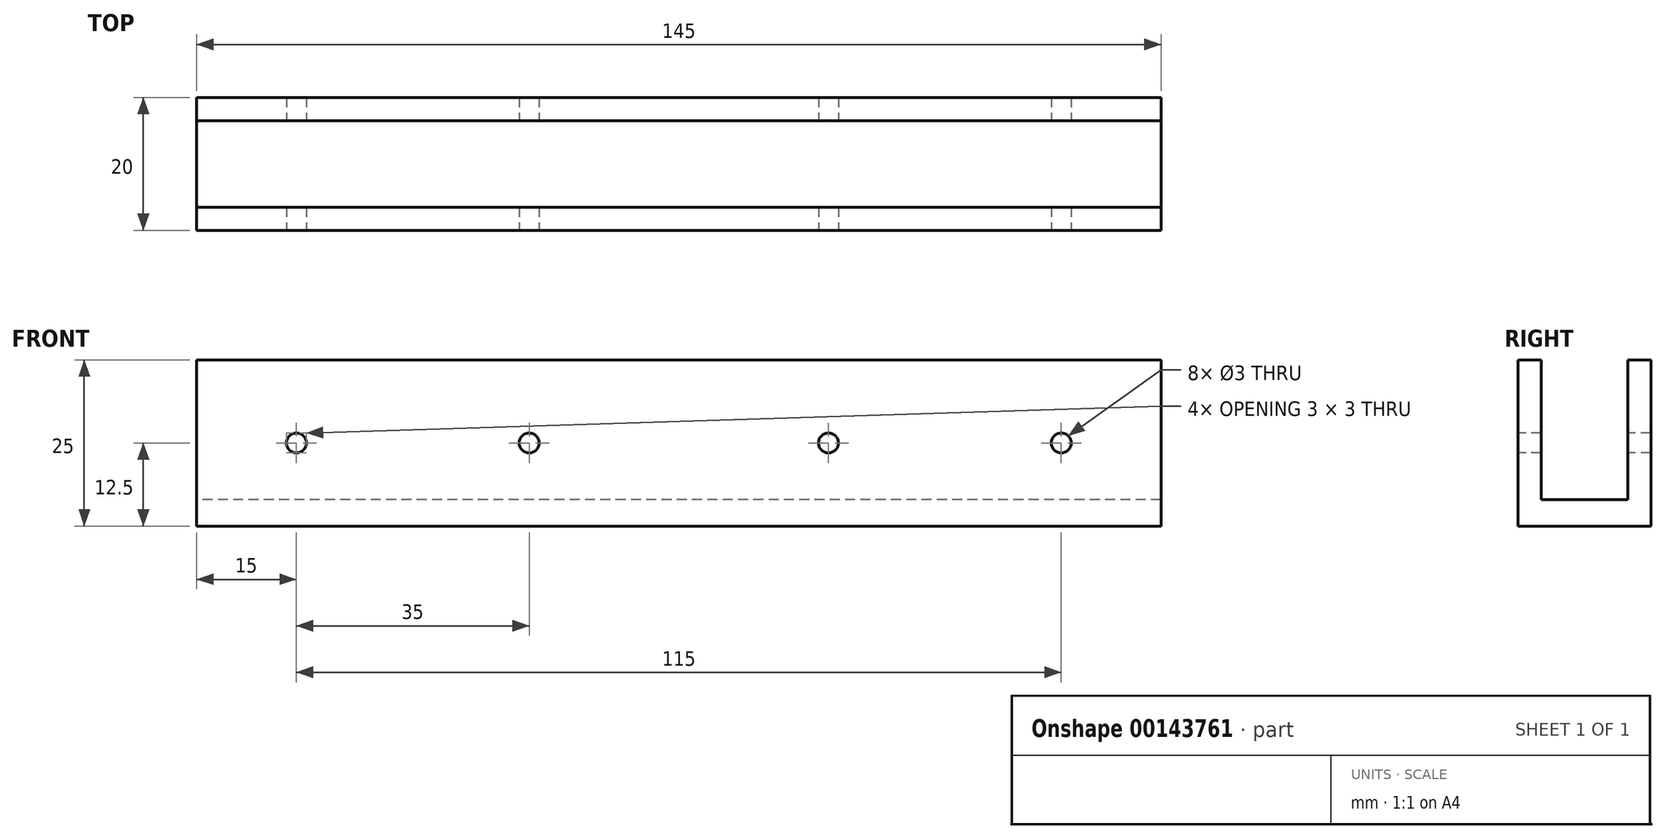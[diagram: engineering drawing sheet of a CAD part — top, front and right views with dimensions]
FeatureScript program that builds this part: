
annotation { "Feature Type Name" : "Feature", "Feature Type Description" : "" }
export const myFeature = defineFeature(function(context is Context, id is Id, definition is map)
    precondition{}
    {
        {
            var Q0;
            Q0=qCreatedBy(makeId("Right.planeOp"),FACE);
            var sketch = newSketch(context, id + "F0", { "sketchPlane" : qUnion([Q0])});
            skLineSegment(sketch, "E0", {"start": v(0, 0) * mm, "end": v(-10, 0) * mm});
            skLineSegment(sketch, "E1", {"start": v(-10, 0) * mm, "end": v(-10, 25) * mm});
            skLineSegment(sketch, "E2", {"start": v(-10, 25) * mm, "end": v(-6.5, 25) * mm});
            skLineSegment(sketch, "E3", {"start": v(-6.5, 25) * mm, "end": v(-6.5, 4) * mm});
            skLineSegment(sketch, "E4", {"start": v(-6.5, 4) * mm, "end": v(0, 4) * mm});
            skLineSegment(sketch, "E5.MirrorCS", {"start": v(6.5, 4) * mm, "end": v(0, 4) * mm});
            skLineSegment(sketch, "E6.MirrorCS", {"start": v(6.5, 25) * mm, "end": v(6.5, 4) * mm});
            skLineSegment(sketch, "E7.MirrorCS", {"start": v(10, 25) * mm, "end": v(6.5, 25) * mm});
            skLineSegment(sketch, "E8.MirrorCS", {"start": v(10, 0) * mm, "end": v(10, 25) * mm});
            skLineSegment(sketch, "E9.MirrorCS", {"start": v(0, 0) * mm, "end": v(10, 0) * mm});
            skSolve(sketch);
        }
        {
            var Q0;
            Q0 = qSketchRegion(id + "F0", true);
            extrude(context, id + "F1", {"entities" : qUnion([Q0]), "depth" : 145 * mm});
        }
        {
            var Q0;
            Q0=makeQuery(id+"F1.opExtrude","SWEPT_FACE",FACE,{"disambiguationData":[OSD([sQuery(id+"F0.wireOp",EDGE,"E1")])]});
            var sketch = newSketch(context, id + "F2", { "sketchPlane" : qUnion([Q0])});
            skCircle(sketch, "E10", {"center": v(15, 12.5) * mm, "radius": 1.8 * mm});
            skPoint(sketch, "E10.centerSnap0", {"position": v(0, 12.5) * mm});
            skCircle(sketch, "E11", {"center": v(50, 12.5) * mm, "radius": 2.4 * mm});
            skCircle(sketch, "E12", {"center": v(130, 12.5) * mm, "radius": 1.6 * mm});
            skCircle(sketch, "E13", {"center": v(95, 12.5) * mm, "radius": 1.81 * mm});
            skSolve(sketch);
        }
        {
            var Q0;
            Q0=sQuery(id+"F2.wireOp",VERTEX,"E10.center");
            var Q1;
            Q1=sQuery(id+"F2.wireOp",VERTEX,"E11.center");
            var Q2;
            Q2=sQuery(id+"F2.wireOp",VERTEX,"E13.center");
            var Q3;
            Q3=sQuery(id+"F2.wireOp",VERTEX,"E12.center");
            var Q4;
            Q4=makeQuery(id+"F1.opExtrude","SWEPT_BODY",BODY,{"disambiguationData":[OSD([sQuery(id+"F0.wireOp",EDGE,"E0"),sQuery(id+"F0.wireOp",EDGE,"E1"),sQuery(id+"F0.wireOp",EDGE,"E2"),sQuery(id+"F0.wireOp",EDGE,"E3"),sQuery(id+"F0.wireOp",EDGE,"E4"),sQuery(id+"F0.wireOp",EDGE,"E5.MirrorCS"),sQuery(id+"F0.wireOp",EDGE,"E6.MirrorCS"),sQuery(id+"F0.wireOp",EDGE,"E7.MirrorCS"),sQuery(id+"F0.wireOp",EDGE,"E8.MirrorCS"),sQuery(id+"F0.wireOp",EDGE,"E9.MirrorCS")])]});
            hole(context, id + "F3", {"style" : HoleStyle.SIMPLE, "endStyle" : HoleEndStyle.THROUGH, "holeDiameter" : 3 * mm, "locations" : qUnion([Q0, Q1, Q2, Q3]), "scope" : qUnion([Q4]), "isTappedThrough" : true});
        }
    });
